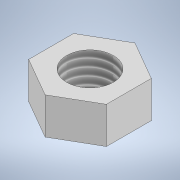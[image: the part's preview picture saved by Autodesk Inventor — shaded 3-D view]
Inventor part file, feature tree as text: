
AUTODESK INVENTOR PART (.ipt)
format: ipt  version: 2020.2 (Build 242310000, 310)  size: 106,496 bytes
history: native  units: mm
features: extrude x2, sketch x2, thread x1
ambient origin geometry x8: Origin, YZ Plane, XZ Plane, XY Plane, X Axis, Y Axis, Z Axis, Center Point
bodies: Solido1 (feature_tree)
feature tree (5):
  extrude  "Estrusione1"  Depth=10.0mm
  extrude  "Estrusione2"  Depth=4.7mm TaperAngle=0.0deg
  thread  "Filettatura1"
  sketch  "Schizzo1"
  sketch  "Schizzo2"
